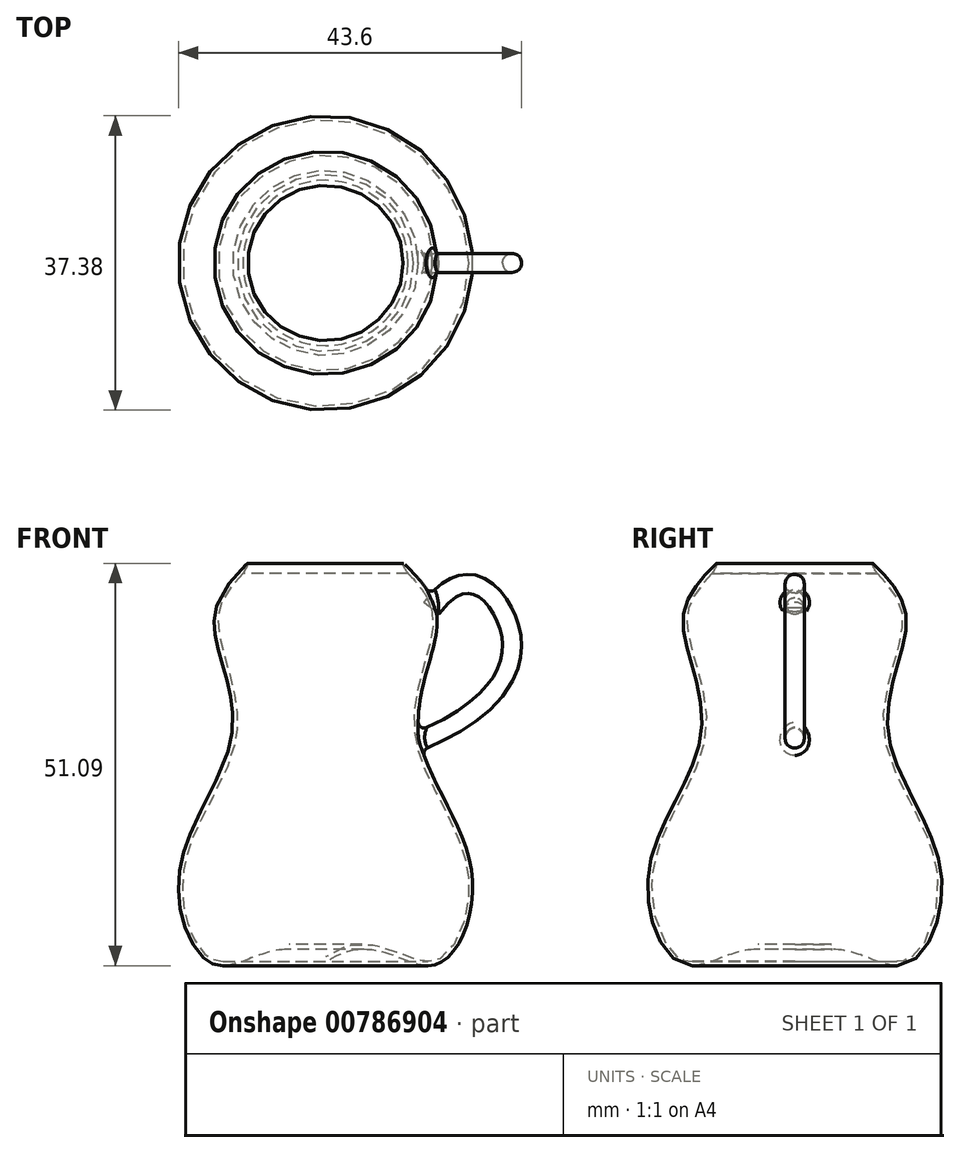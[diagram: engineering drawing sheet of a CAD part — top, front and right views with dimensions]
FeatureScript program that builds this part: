
annotation { "Feature Type Name" : "Feature", "Feature Type Description" : "" }
export const myFeature = defineFeature(function(context is Context, id is Id, definition is map)
    precondition{}
    {
        {
            var Q0;
            Q0=qCreatedBy(makeId("Front.planeOp"),FACE);
            var sketch = newSketch(context, id + "F0", { "sketchPlane" : qUnion([Q0])});
            skFitSpline(sketch, "E0", {"points": [v(10.53, 50.94) * mm, v(14.59, 42.77) * mm, v(12.33, 29.38) * mm, v(19.05, 11.67) * mm, v(14.02, 0) * mm, v(0, 0) * mm], "startDerivative": vector(58.43, -58.03) * mm, "endDerivative": vector(-88.95, -70.69) * mm});
            skFitSpline(sketch, "E1.0", {"points": [v(10.15, 50.56) * mm, v(10.76, 49.96) * mm, v(11.8, 48.86) * mm, v(12.95, 47.38) * mm, v(13.69, 46.02) * mm, v(14.07, 44.7) * mm, v(14.13, 43.5) * mm, v(14.02, 42.45) * mm, v(13.82, 41.3) * mm, v(13.42, 39.75) * mm, v(12.84, 37.7) * mm, v(12.26, 35.53) * mm, v(11.81, 33.26) * mm, v(11.66, 31.32) * mm, v(11.73, 29.74) * mm, v(11.9, 28.56) * mm, v(12.2, 27.39) * mm, v(12.7, 25.84) * mm, v(13.5, 23.93) * mm, v(14.65, 21.64) * mm, v(15.84, 19.35) * mm, v(16.96, 17.03) * mm, v(17.73, 15.06) * mm, v(18.2, 13.47) * mm, v(18.45, 12.26) * mm, v(18.6, 11.03) * mm, v(18.65, 9.37) * mm, v(18.45, 7.3) * mm, v(17.86, 4.98) * mm, v(16.97, 2.98) * mm, v(15.83, 1.47) * mm, v(14.88, 0.8) * mm, v(14.23, 0.58) * mm, v(13.9, 0.51) * mm, v(13.57, 0.49) * mm, v(13.1, 0.5) * mm, v(12.45, 0.61) * mm, v(11.31, 0.95) * mm, v(9.73, 1.59) * mm, v(7.58, 2.33) * mm, v(5.17, 2.68) * mm, v(2.52, 2.24) * mm, v(0.63, 1.18) * mm, v(-0.33, 0.42) * mm]});
            skFitSpline(sketch, "E2", {"points": [v(11.16, 49.52) * mm, v(10.33, 50.94) * mm, v(10.53, 50.94) * mm], "startDerivative": vector(-1.12, 1.03) * mm, "endDerivative": vector(2.16, -2.12) * mm});
            skLineSegment(sketch, "E3", {"start": v(0, 0) * mm, "end": v(0, 0.68) * mm});
            skLineSegment(sketch, "E4", {"start": v(0.46, 3.86) * mm, "end": v(0.46, -1.98) * mm});
            skSolve(sketch);
        }
        {
            var Q0;
            {var subQ0=sQuery(id+"F0.wireOp",EDGE,"E2");Q0=makeQuery(id+"F0.imprint","IMPRINT",FACE,{"disambiguationData":[TD([[makeQuery(id+"F0.imprint","IMPRINT",EDGE,{"derivedFrom":subQ0}),-1.0]])]});}
            var Q1;
            Q1=sQuery(id+"F0.wireOp",EDGE,"E4");
            revolve(context, id + "F1", {"surfaceOperationType" : NewSurfaceOperationType.NEW, "entities" : qUnion([Q0]), "axis" : qUnion([Q1]), "revolveType" : RevolveType.FULL});
        }
        {
            var Q0;
            Q0=qCreatedBy(makeId("Front.planeOp"),FACE);
            var sketch = newSketch(context, id + "F2", { "sketchPlane" : qUnion([Q0])});
            skFitSpline(sketch, "E5", {"points": [v(13.9, 45.4) * mm, v(23.23, 44.53) * mm, v(12.27, 28.44) * mm], "startDerivative": vector(30.48, 40.62) * mm, "endDerivative": vector(-59.61, -24.84) * mm});
            skSolve(sketch);
        }
        {
            var Q0;
            Q0=sQuery(id+"F2.wireOp",EDGE,"E5");
            var Q1;
            Q1=sQuery(id+"F2.wireOp",VERTEX,"E5.end");
            cPlane(context, id + "F3", {"entities" : qUnion([Q0, Q1]), "cplaneType" : CPlaneType.CURVE_POINT, "offset" : 25.4 * mm, "width" : 152.4 * mm, "height" : 152.4 * mm});
        }
        {
            var Q0;
            Q0=qCreatedBy(id+"F3.planeOp",FACE);
            var sketch = newSketch(context, id + "F4", { "sketchPlane" : qUnion([Q0])});
            skCircle(sketch, "E6", {"center": v(0, 21.54) * mm, "radius": 1.2 * mm});
            skSolve(sketch);
        }
        {
            var Q0;
            Q0=makeQuery(id+"F4.imprint","IMPRINT",FACE,{"disambiguationData":[TD([[makeQuery(id+"F4.imprint","IMPRINT",EDGE,{"derivedFrom":sQuery(id+"F4.wireOp",EDGE,"E6")}),1.0]])]});
            var Q1;
            Q1=sQuery(id+"F2.wireOp",EDGE,"E5");
            sweep(context, id + "F5", {"operationType" : NewBodyOperationType.ADD, "profiles" : qUnion([Q0]), "path" : qUnion([Q1])});
        }
        {
            var Q0;
            Q0=makeQuery(id+"F5.boolean.opBoolean","INTERSECT",EDGE,{"disambiguationData":[OD(0.0)],"derivedFrom":[makeQuery(id+"F1.opRevolve","SWEPT_FACE",FACE,{"disambiguationData":[OSD([sQuery(id+"F0.wireOp",EDGE,"E0")])]}),makeQuery(id+"F5.opSweep","SWEPT_FACE",FACE,{"disambiguationData":[OSD([sQuery(id+"F2.wireOp",EDGE,"E5"),sQuery(id+"F4.wireOp",EDGE,"E6")])]})]});
            var Q1;
            Q1=makeQuery(id+"F5.boolean.opBoolean","INTERSECT",EDGE,{"disambiguationData":[OD(1.0)],"derivedFrom":[makeQuery(id+"F1.opRevolve","SWEPT_FACE",FACE,{"disambiguationData":[OSD([sQuery(id+"F0.wireOp",EDGE,"E0")])]}),makeQuery(id+"F5.opSweep","SWEPT_FACE",FACE,{"disambiguationData":[OSD([sQuery(id+"F2.wireOp",EDGE,"E5"),sQuery(id+"F4.wireOp",EDGE,"E6")])]})]});
            fillet(context, id + "F6", {"entities" : qUnion([Q0, Q1]), "radius" : 0.76 * mm, "tangentPropagation" : true, "allowEdgeOverflow" : false});
        }
    });
